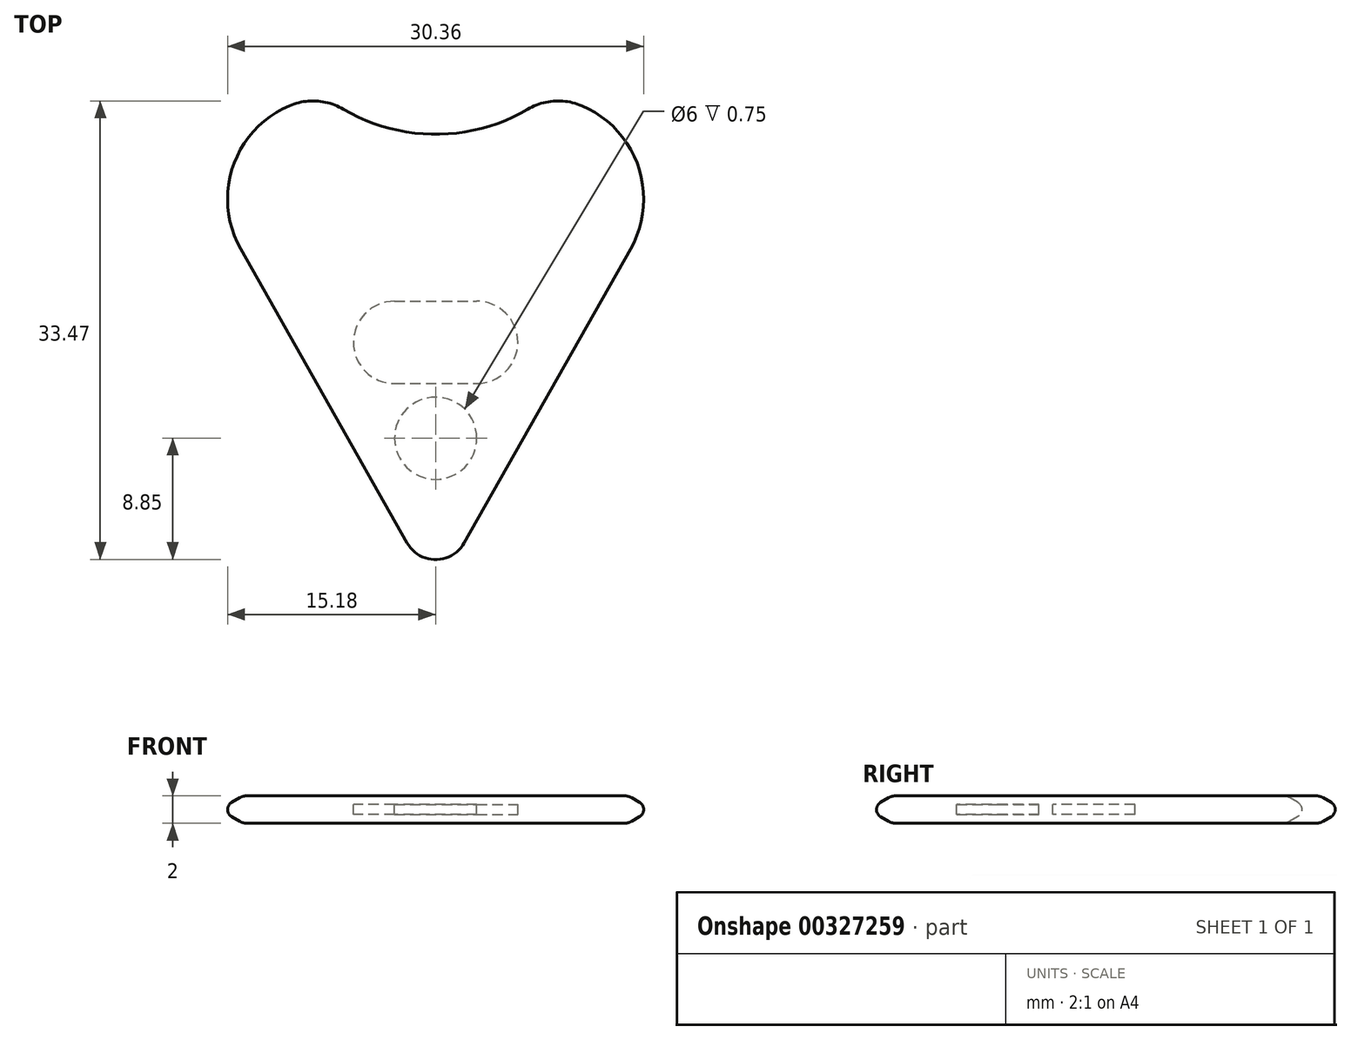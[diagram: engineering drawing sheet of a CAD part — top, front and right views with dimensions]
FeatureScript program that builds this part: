
annotation { "Feature Type Name" : "Feature", "Feature Type Description" : "" }
export const myFeature = defineFeature(function(context is Context, id is Id, definition is map)
    precondition{}
    {
        {
            var Q0;
            Q0=qCreatedBy(makeId("Top.planeOp"),FACE);
            var sketch = newSketch(context, id + "F0", { "sketchPlane" : qUnion([Q0])});
            skLineSegment(sketch, "E0", {"start": v(-7.78, 12.45) * mm, "end": v(7.78, 12.45) * mm});
            skLineSegment(sketch, "E1", {"start": v(14.74, 0.52) * mm, "end": v(2.61, -20.93) * mm});
            skLineSegment(sketch, "E2", {"start": v(-2.61, -20.93) * mm, "end": v(-14.74, 0.52) * mm});
            skPoint(sketch, "E3.visualSharp", {"position": v(-21.5, 12.45) * mm});
            skArc(sketch, "E3.filletArc", {"start": v(-7.78, 12.45) * mm, "mid": v(-14.7, 8.48) * mm, "end": v(-14.74, 0.52) * mm});
            skPoint(sketch, "E4.visualSharp", {"position": v(21.5, 12.45) * mm});
            skArc(sketch, "E4.filletArc", {"start": v(14.74, 0.52) * mm, "mid": v(14.7, 8.48) * mm, "end": v(7.78, 12.45) * mm});
            skPoint(sketch, "E5.visualSharp", {"position": v(0, -25.55) * mm});
            skArc(sketch, "E5.filletArc", {"start": v(-2.61, -20.93) * mm, "mid": v(0, -22.45) * mm, "end": v(2.61, -20.93) * mm});
            skSolve(sketch);
        }
        {
            var Q0;
            Q0=makeQuery(id+"F0.imprint","IMPRINT",FACE,{"disambiguationData":[TD([[makeQuery(id+"F0.imprint","IMPRINT",EDGE,{"derivedFrom":sQuery(id+"F0.wireOp",EDGE,"E0")}),-1.0]])]});
            extrude(context, id + "F1", {"entities" : qUnion([Q0]), "endBound" : BoundingType.SYMMETRIC, "depth" : 2 * mm});
        }
        {
            var Q0;
            Q0=makeQuery(id+"F1.opExtrude","CAP_FACE",FACE,{"disambiguationData":[OSD([sQuery(id+"F0.wireOp",EDGE,"E0"),sQuery(id+"F0.wireOp",EDGE,"E1"),sQuery(id+"F0.wireOp",EDGE,"E2"),sQuery(id+"F0.wireOp",EDGE,"E3.filletArc"),sQuery(id+"F0.wireOp",EDGE,"E4.filletArc"),sQuery(id+"F0.wireOp",EDGE,"E5.filletArc")])],"isStart":false});
            var sketch = newSketch(context, id + "F2", { "sketchPlane" : qUnion([Q0])});
            skArc(sketch, "E6", {"start": v(-7.78, 12.45) * mm, "mid": v(0, 9.78) * mm, "end": v(7.78, 12.45) * mm});
            skLineSegment(sketch, "E7.0", {"start": v(-7.78, 12.45) * mm, "end": v(7.78, 12.45) * mm});
            skSolve(sketch);
        }
        {
            var Q0;
            Q0=qSketchRegion(id+"F2",true);
            extrude(context, id + "F3", {"entities" : qUnion([Q0]), "operationType" : NewBodyOperationType.REMOVE, "oppositeDirection" : true, "depth" : 25 * mm});
        }
        {
            var Q0;
            {var subQ0=sQuery(id+"F0.wireOp",EDGE,"E3.filletArc");Q0=makeQuery(id+"F3.boolean.opBoolean","MERGE",EDGE,{"derivedFrom":[makeQuery(id+"F1.opExtrude","SWEPT_EDGE",EDGE,{"disambiguationData":[OSD([sQuery(id+"F0.wireOp",EDGE,"E0"),subQ0])]}),makeQuery(id+"F3.opExtrude","SWEPT_EDGE",EDGE,{"disambiguationData":[OSD([subQ0,sQuery(id+"F2.wireOp",EDGE,"E6"),sQuery(id+"F2.wireOp",EDGE,"E7.0")])]})]});}
            var Q1;
            {var subQ0=sQuery(id+"F0.wireOp",EDGE,"E4.filletArc");Q1=makeQuery(id+"F3.boolean.opBoolean","MERGE",EDGE,{"derivedFrom":[makeQuery(id+"F1.opExtrude","SWEPT_EDGE",EDGE,{"disambiguationData":[OSD([sQuery(id+"F0.wireOp",EDGE,"E0"),subQ0])]}),makeQuery(id+"F3.opExtrude","SWEPT_EDGE",EDGE,{"disambiguationData":[OSD([subQ0,sQuery(id+"F2.wireOp",EDGE,"E6"),sQuery(id+"F2.wireOp",EDGE,"E7.0")])]})]});}
            fillet(context, id + "F4", {"entities" : qUnion([Q0, Q1]), "radius" : 5 * mm, "tangentPropagation" : true, "allowEdgeOverflow" : false});
        }
        {
            var Q0;
            Q0=makeQuery(id+"F1.opExtrude","CAP_EDGE",EDGE,{"disambiguationData":[OSD([sQuery(id+"F0.wireOp",EDGE,"E1")])],"isStart":false});
            var Q1;
            Q1=makeQuery(id+"F1.opExtrude","CAP_EDGE",EDGE,{"disambiguationData":[OSD([sQuery(id+"F0.wireOp",EDGE,"E1")])],"isStart":true});
            chamfer(context, id + "F5", {"entities" : qUnion([Q0, Q1]), "chamferType" : ChamferType.OFFSET_ANGLE, "width" : 1 * mm, "oppositeDirection" : false, "angle" : 60 * degree, "tangentPropagation" : true});
        }
        {
            var Q0;
            {var subQ0=sQuery(id+"F0.wireOp",EDGE,"E2");Q0=makeQuery(id+"F5.opChamfer","BLEND_EDGE",EDGE,{"blendedFrom":[makeQuery(id+"F1.opExtrude","CAP_EDGE",EDGE,{"disambiguationData":[OSD([subQ0])],"isStart":false}),makeQuery(id+"F1.opExtrude","CAP_FACE",FACE,{"disambiguationData":[OSD([sQuery(id+"F0.wireOp",EDGE,"E0"),sQuery(id+"F0.wireOp",EDGE,"E1"),subQ0,sQuery(id+"F0.wireOp",EDGE,"E3.filletArc"),sQuery(id+"F0.wireOp",EDGE,"E4.filletArc"),sQuery(id+"F0.wireOp",EDGE,"E5.filletArc")])],"isStart":false})],"blendedInto":[makeQuery(id+"F1.opExtrude","CAP_FACE",FACE,{"disambiguationData":[OSD([sQuery(id+"F0.wireOp",EDGE,"E0"),sQuery(id+"F0.wireOp",EDGE,"E1"),subQ0,sQuery(id+"F0.wireOp",EDGE,"E3.filletArc"),sQuery(id+"F0.wireOp",EDGE,"E4.filletArc"),sQuery(id+"F0.wireOp",EDGE,"E5.filletArc")])],"isStart":false})]});}
            var Q1;
            {var subQ0=sQuery(id+"F0.wireOp",EDGE,"E1");Q1=makeQuery(id+"F5.opChamfer","BLEND_EDGE",EDGE,{"blendedFrom":[makeQuery(id+"F1.opExtrude","CAP_EDGE",EDGE,{"disambiguationData":[OSD([subQ0])],"isStart":true}),makeQuery(id+"F1.opExtrude","CAP_FACE",FACE,{"disambiguationData":[OSD([sQuery(id+"F0.wireOp",EDGE,"E0"),subQ0,sQuery(id+"F0.wireOp",EDGE,"E2"),sQuery(id+"F0.wireOp",EDGE,"E3.filletArc"),sQuery(id+"F0.wireOp",EDGE,"E4.filletArc"),sQuery(id+"F0.wireOp",EDGE,"E5.filletArc")])],"isStart":true})],"blendedInto":[makeQuery(id+"F1.opExtrude","CAP_FACE",FACE,{"disambiguationData":[OSD([sQuery(id+"F0.wireOp",EDGE,"E0"),subQ0,sQuery(id+"F0.wireOp",EDGE,"E2"),sQuery(id+"F0.wireOp",EDGE,"E3.filletArc"),sQuery(id+"F0.wireOp",EDGE,"E4.filletArc"),sQuery(id+"F0.wireOp",EDGE,"E5.filletArc")])],"isStart":true})]});}
            fillet(context, id + "F6", {"entities" : qUnion([Q0, Q1]), "radius" : 1 * mm, "tangentPropagation" : true, "allowEdgeOverflow" : false});
        }
        {
            var Q0;
            Q0=qCreatedBy(makeId("Top.planeOp"),FACE);
            var sketch = newSketch(context, id + "F7", { "sketchPlane" : qUnion([Q0])});
            skCircle(sketch, "E8", {"center": v(0, -13) * mm, "radius": 3 * mm});
            skArc(sketch, "E9", {"start": v(3, -9) * mm, "mid": v(6, -6) * mm, "end": v(3, -3) * mm});
            skArc(sketch, "E10", {"start": v(-3, -3) * mm, "mid": v(-6, -6) * mm, "end": v(-3, -9) * mm});
            skLineSegment(sketch, "E11", {"start": v(-3, -3) * mm, "end": v(3, -3) * mm});
            skLineSegment(sketch, "E12", {"start": v(-3, -9) * mm, "end": v(3, -9) * mm});
            skSolve(sketch);
        }
        {
            var Q0;
            Q0=qSketchRegion(id+"F7",true);
            extrude(context, id + "F8", {"entities" : qUnion([Q0]), "operationType" : NewBodyOperationType.REMOVE, "endBound" : BoundingType.SYMMETRIC, "oppositeDirection" : true, "depth" : 0.75 * mm});
        }
        {
            var Q0;
            {var subQ0=sQuery(id+"F0.wireOp",EDGE,"E2");Q0=makeQuery(id+"F5.opChamfer","BLEND_EDGE",EDGE,{"blendedFrom":[makeQuery(id+"F1.opExtrude","CAP_EDGE",EDGE,{"disambiguationData":[OSD([subQ0])],"isStart":true}),makeQuery(id+"F1.opExtrude","CAP_EDGE",EDGE,{"disambiguationData":[OSD([subQ0])],"isStart":false})],"blendedInto":[]});}
            fillet(context, id + "F9", {"entities" : qUnion([Q0]), "radius" : 0.6 * mm, "tangentPropagation" : true, "allowEdgeOverflow" : false});
        }
    });
